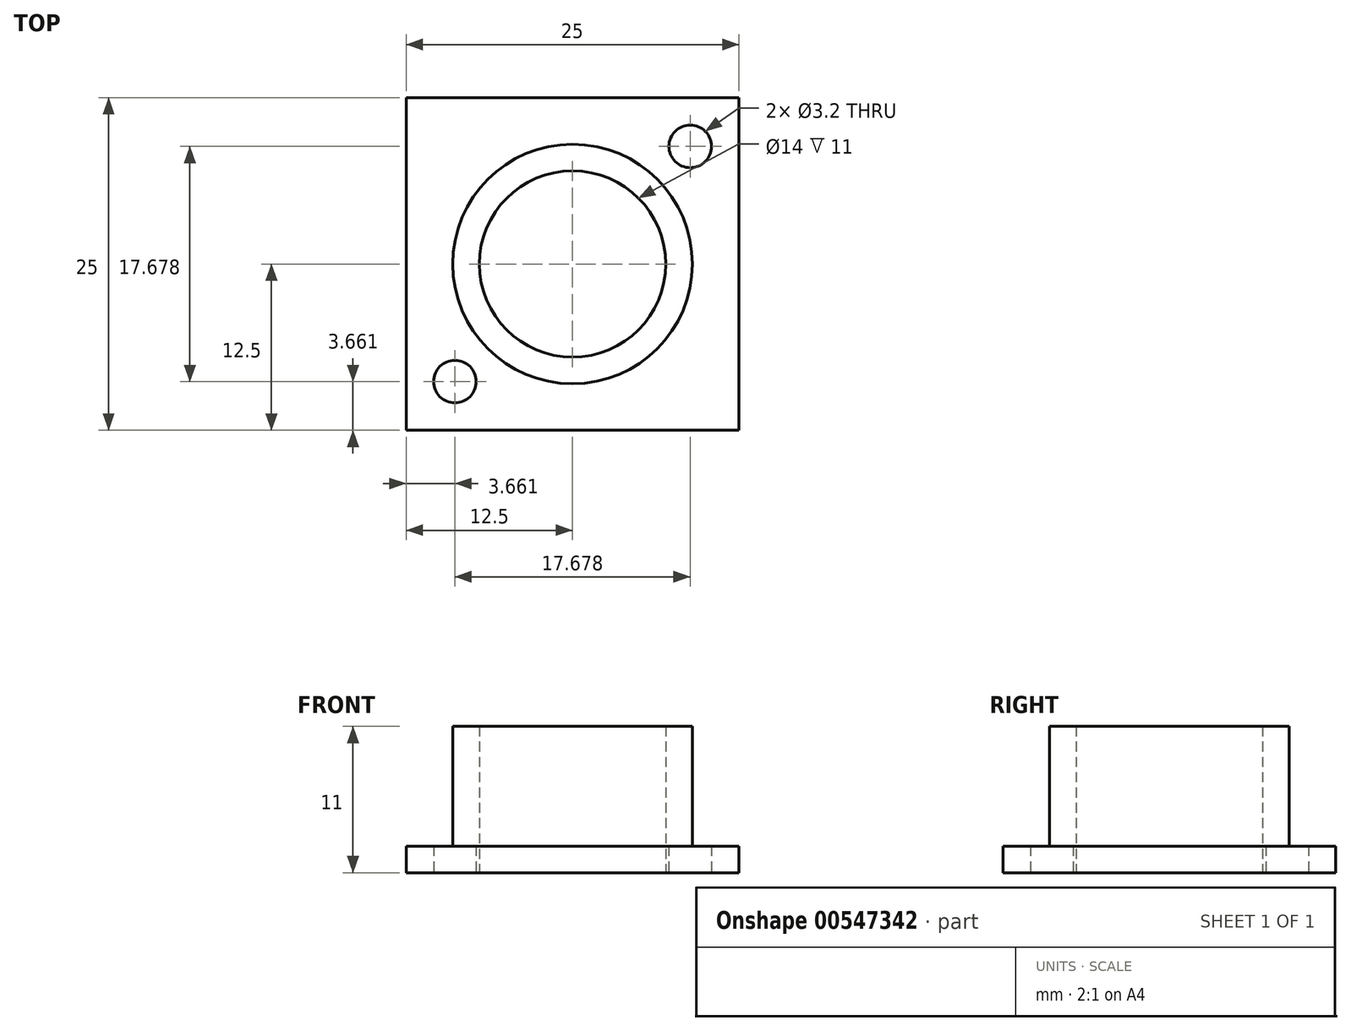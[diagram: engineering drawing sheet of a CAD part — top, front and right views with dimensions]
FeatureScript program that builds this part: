
annotation { "Feature Type Name" : "Feature", "Feature Type Description" : "" }
export const myFeature = defineFeature(function(context is Context, id is Id, definition is map)
    precondition{}
    {
        {
            var Q0;
            Q0=qCreatedBy(makeId("Top.planeOp"),FACE);
            var sketch = newSketch(context, id + "F0", { "sketchPlane" : qUnion([Q0])});
            skLineSegment(sketch, "E0.bottom", {"start": v(12.5, 12.5) * mm, "end": v(-12.5, 12.5) * mm});
            skLineSegment(sketch, "E0.top", {"start": v(12.5, -12.5) * mm, "end": v(-12.5, -12.5) * mm});
            skLineSegment(sketch, "E0.left", {"start": v(12.5, 12.5) * mm, "end": v(12.5, -12.5) * mm});
            skLineSegment(sketch, "E0.right", {"start": v(-12.5, 12.5) * mm, "end": v(-12.5, -12.5) * mm});
            skPoint(sketch, "E0.middle", {"position": v(0, 0) * mm});
            skLineSegment(sketch, "E1", {"start": v(-12.5, -12.5) * mm, "end": v(12.5, 12.5) * mm, "construction": true});
            skCircle(sketch, "E2", {"center": v(8.84, 8.84) * mm, "radius": 1.6 * mm});
            skLineSegment(sketch, "E3", {"start": v(0, 0) * mm, "end": v(-12.5, 12.5) * mm, "construction": true});
            skCircle(sketch, "E4.MirrorC", {"center": v(-8.84, -8.84) * mm, "radius": 1.6 * mm});
            skCircle(sketch, "E5", {"center": v(0, 0) * mm, "radius": 7 * mm});
            skSolve(sketch);
        }
        {
            var Q0;
            Q0 = qSketchRegion(id + "F0", true);
            extrude(context, id + "F1", {"entities" : qUnion([Q0]), "depth" : 2 * mm, "offsetDistance" : 25 * mm});
        }
        {
            var Q0;
            Q0=makeQuery(id+"F1.opExtrude","CAP_FACE",FACE,{"disambiguationData":[OSD([sQuery(id+"F0.wireOp",EDGE,"E0.bottom"),sQuery(id+"F0.wireOp",EDGE,"E0.top"),sQuery(id+"F0.wireOp",EDGE,"E0.left"),sQuery(id+"F0.wireOp",EDGE,"E0.right"),sQuery(id+"F0.wireOp",EDGE,"E2"),sQuery(id+"F0.wireOp",EDGE,"E4.MirrorC"),sQuery(id+"F0.wireOp",EDGE,"E5")])],"isStart":false});
            var sketch = newSketch(context, id + "F2", { "sketchPlane" : qUnion([Q0])});
            skCircle(sketch, "E6", {"center": v(0, 0) * mm, "radius": 9 * mm});
            skCircle(sketch, "E7", {"center": v(0, 0) * mm, "radius": 7 * mm});
            skSolve(sketch);
        }
        {
            var Q0;
            Q0 = qSketchRegion(id + "F2", true);
            extrude(context, id + "F3", {"entities" : qUnion([Q0]), "operationType" : NewBodyOperationType.ADD, "depth" : 9 * mm, "offsetDistance" : 25 * mm});
        }
    });
